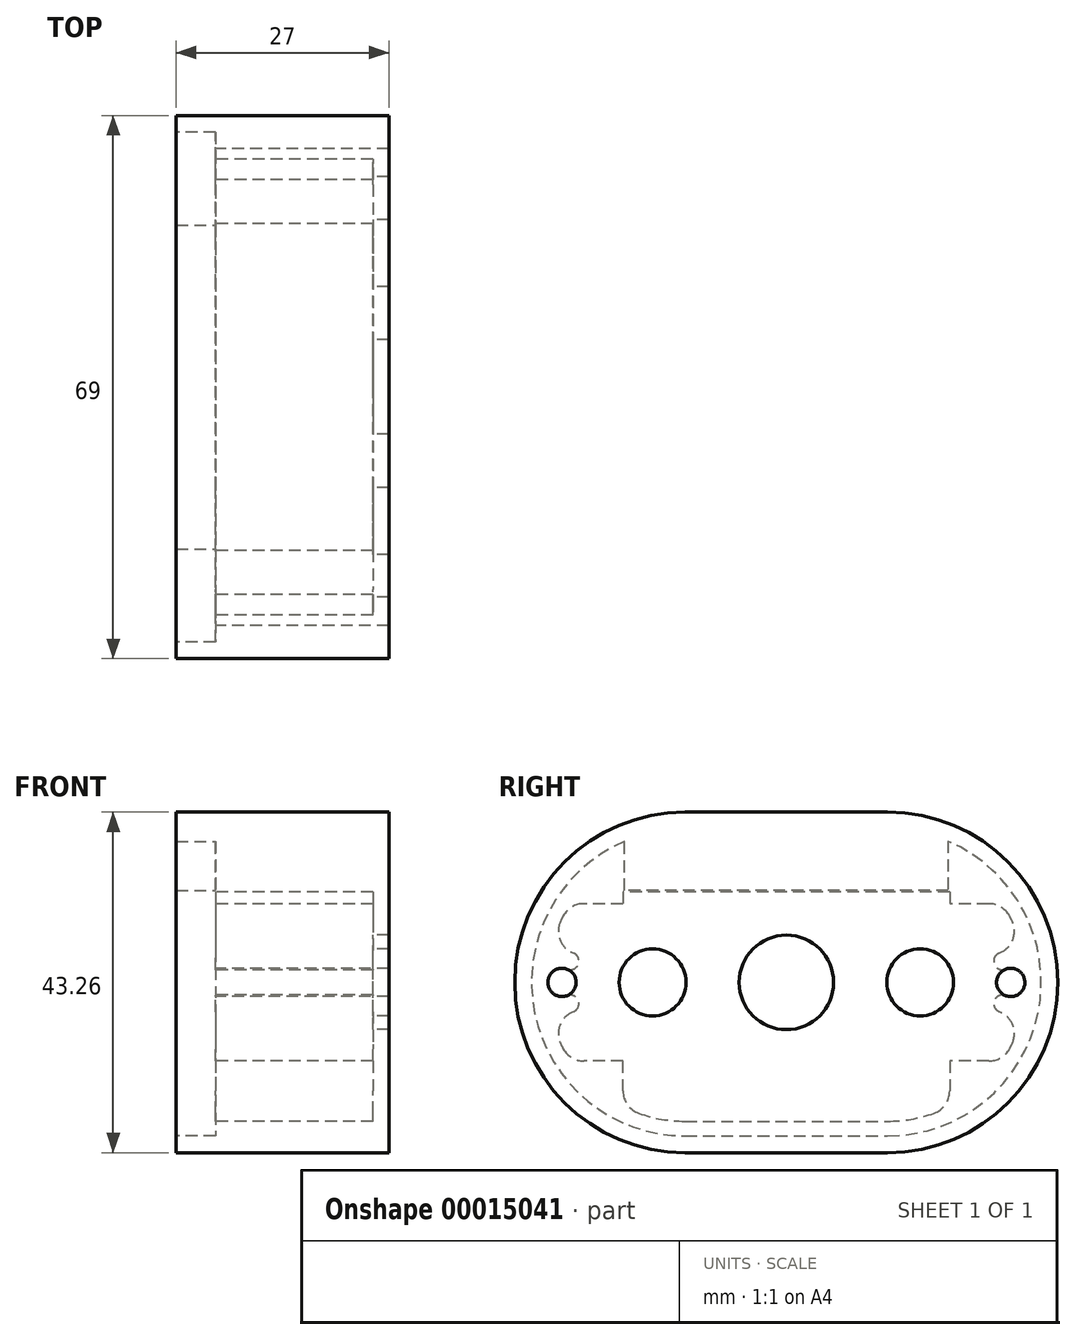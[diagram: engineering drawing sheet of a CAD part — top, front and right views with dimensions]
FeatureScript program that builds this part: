
annotation { "Feature Type Name" : "Feature", "Feature Type Description" : "" }
export const myFeature = defineFeature(function(context is Context, id is Id, definition is map)
    precondition{}
    {
        {
            var Q0;
            Q0=qCreatedBy(makeId("Right.planeOp"),FACE);
            var sketch = newSketch(context, id + "F0", { "sketchPlane" : qUnion([Q0])});
            skLineSegment(sketch, "E0.rect.bottom", {"start": v(23.75, -10) * mm, "end": v(-23.75, -10) * mm});
            skLineSegment(sketch, "E0.rect.top", {"start": v(23.75, 10) * mm, "end": v(-23.75, 10) * mm});
            skLineSegment(sketch, "E0.rect.left", {"start": v(23.75, -10) * mm, "end": v(23.75, 10) * mm});
            skLineSegment(sketch, "E0.rect.right", {"start": v(-23.75, -10) * mm, "end": v(-23.75, 10) * mm});
            skLineSegment(sketch, "E1.bottom", {"start": v(-23.75, 10) * mm, "end": v(23.75, 10) * mm});
            skLineSegment(sketch, "E1.top", {"start": v(-23.75, 12.1) * mm, "end": v(23.75, 12.1) * mm});
            skLineSegment(sketch, "E1.left", {"start": v(-23.75, 10) * mm, "end": v(-23.75, 12.1) * mm});
            skLineSegment(sketch, "E1.right", {"start": v(23.75, 10) * mm, "end": v(23.75, 12.1) * mm});
            skLineSegment(sketch, "E2.bottom", {"start": v(-23.75, -10) * mm, "end": v(23.75, -10) * mm});
            skLineSegment(sketch, "E2.top", {"start": v(-23.75, -12.1) * mm, "end": v(23.75, -12.1) * mm});
            skLineSegment(sketch, "E2.left", {"start": v(-23.75, -10) * mm, "end": v(-23.75, -12.1) * mm});
            skLineSegment(sketch, "E2.right", {"start": v(23.75, -10) * mm, "end": v(23.75, -12.1) * mm});
            skLineSegment(sketch, "E3", {"start": v(-23.75, 10) * mm, "end": v(0, 0) * mm, "construction": true});
            skLineSegment(sketch, "E4", {"start": v(0, 0) * mm, "end": v(23.75, -10) * mm, "construction": true});
            skLineSegment(sketch, "E5", {"start": v(-23.75, -10) * mm, "end": v(-20.75, -10) * mm});
            skLineSegment(sketch, "E6", {"start": v(-20.75, -10) * mm, "end": v(-20.75, -8) * mm});
            skLineSegment(sketch, "E7", {"start": v(-20.75, -8) * mm, "end": v(-25.75, -8) * mm});
            skLineSegment(sketch, "E8", {"start": v(-25.75, -8) * mm, "end": v(-25.75, -14.1) * mm});
            skLineSegment(sketch, "E9", {"start": v(-25.75, -14.1) * mm, "end": v(-20.75, -14.1) * mm});
            skLineSegment(sketch, "E10", {"start": v(-20.75, -14.1) * mm, "end": v(-20.75, -17.1) * mm});
            skLineSegment(sketch, "E11", {"start": v(-20.75, -17.1) * mm, "end": v(20.75, -17.1) * mm});
            skLineSegment(sketch, "E12", {"start": v(20.75, -17.1) * mm, "end": v(20.75, -14.1) * mm});
            skLineSegment(sketch, "E13", {"start": v(20.75, -14.1) * mm, "end": v(25.75, -14.1) * mm});
            skLineSegment(sketch, "E14", {"start": v(25.75, -14.1) * mm, "end": v(25.75, -8) * mm});
            skLineSegment(sketch, "E15", {"start": v(25.75, -8) * mm, "end": v(20.75, -8) * mm});
            skLineSegment(sketch, "E16", {"start": v(20.75, -8) * mm, "end": v(20.75, -10) * mm});
            skLineSegment(sketch, "E17", {"start": v(-20.75, 10) * mm, "end": v(-20.75, 8) * mm});
            skLineSegment(sketch, "E18", {"start": v(-20.75, 8) * mm, "end": v(-25.75, 8) * mm});
            skLineSegment(sketch, "E19", {"start": v(-25.75, 8) * mm, "end": v(-25.75, 14.1) * mm});
            skLineSegment(sketch, "E20", {"start": v(-25.75, 14.1) * mm, "end": v(-20.75, 14.1) * mm});
            skLineSegment(sketch, "E21", {"start": v(-20.75, 14.1) * mm, "end": v(-20.75, 12.1) * mm});
            skLineSegment(sketch, "E22", {"start": v(20.75, 12.1) * mm, "end": v(20.75, 14.1) * mm});
            skLineSegment(sketch, "E23", {"start": v(20.75, 14.1) * mm, "end": v(25.75, 14.1) * mm});
            skLineSegment(sketch, "E24", {"start": v(25.75, 14.1) * mm, "end": v(25.75, 8) * mm});
            skLineSegment(sketch, "E25", {"start": v(25.75, 8) * mm, "end": v(20.75, 8) * mm});
            skLineSegment(sketch, "E26", {"start": v(20.75, 8) * mm, "end": v(20.75, 10) * mm});
            skCircle(sketch, "E27", {"center": v(-28.5, 0) * mm, "radius": 1.25 * mm});
            skCircle(sketch, "E28", {"center": v(28.5, 0) * mm, "radius": 1.25 * mm});
            skLineSegment(sketch, "E29", {"start": v(-28.5, 0) * mm, "end": v(0, 0) * mm, "construction": true});
            skLineSegment(sketch, "E30", {"start": v(28.5, 0) * mm, "end": v(0, 0) * mm, "construction": true});
            skLineSegment(sketch, "E31.bottom", {"start": v(-25.75, -14.1) * mm, "end": v(25.75, -14.1) * mm});
            skLineSegment(sketch, "E31.top", {"start": v(-25.75, -19.1) * mm, "end": v(25.75, -19.1) * mm});
            skLineSegment(sketch, "E31.left", {"start": v(-25.75, -14.1) * mm, "end": v(-25.75, -19.1) * mm});
            skLineSegment(sketch, "E31.right", {"start": v(25.75, -14.1) * mm, "end": v(25.75, -19.1) * mm});
            skArc(sketch, "E32", {"start": v(-12.87, 19.1) * mm, "mid": v(-31.97, 0) * mm, "end": v(-12.87, -19.1) * mm});
            skArc(sketch, "E33", {"start": v(12.87, -19.1) * mm, "mid": v(31.97, 0) * mm, "end": v(12.87, 19.1) * mm});
            skLineSegment(sketch, "E34", {"start": v(-12.87, 19.1) * mm, "end": v(-12.87, 0) * mm, "construction": true});
            skLineSegment(sketch, "E35", {"start": v(-12.87, -19.1) * mm, "end": v(-12.87, 0) * mm, "construction": true});
            skLineSegment(sketch, "E36", {"start": v(12.87, 0) * mm, "end": v(12.87, 19.1) * mm, "construction": true});
            skLineSegment(sketch, "E37", {"start": v(12.87, 0) * mm, "end": v(12.87, -19.1) * mm, "construction": true});
            skLineSegment(sketch, "E38.rect.bottom", {"start": v(24.5, -9.5) * mm, "end": v(11.5, -9.5) * mm});
            skLineSegment(sketch, "E38.rect.top", {"start": v(24.5, 9.5) * mm, "end": v(11.5, 9.5) * mm});
            skLineSegment(sketch, "E38.rect.left", {"start": v(24.5, -9.5) * mm, "end": v(24.5, 9.5) * mm});
            skLineSegment(sketch, "E38.rect.right", {"start": v(11.5, -9.5) * mm, "end": v(11.5, 9.5) * mm});
            skPoint(sketch, "E38.rect.middle", {"position": v(18, 0) * mm});
            skLineSegment(sketch, "E39.rect.bottom", {"start": v(3.75, -7.75) * mm, "end": v(-18.75, -7.75) * mm});
            skLineSegment(sketch, "E39.rect.top", {"start": v(3.75, 7.75) * mm, "end": v(-18.75, 7.75) * mm});
            skLineSegment(sketch, "E39.rect.left", {"start": v(3.75, -7.75) * mm, "end": v(3.75, 7.75) * mm});
            skLineSegment(sketch, "E39.rect.right", {"start": v(-18.75, -7.75) * mm, "end": v(-18.75, 7.75) * mm});
            skPoint(sketch, "E39.rect.middle", {"position": v(-7.5, 0) * mm});
            skCircle(sketch, "E40", {"center": v(-22.25, 0) * mm, "radius": 1.75 * mm});
            skCircle(sketch, "E41", {"center": v(7.25, 0) * mm, "radius": 1.75 * mm});
            skLineSegment(sketch, "E42", {"start": v(-22.25, 0) * mm, "end": v(-7.5, 0) * mm, "construction": true});
            skLineSegment(sketch, "E43", {"start": v(-7.5, 0) * mm, "end": v(7.25, 0) * mm, "construction": true});
            skLineSegment(sketch, "E44.rect.bottom", {"start": v(10.5, 8.5) * mm, "end": v(-25.5, 8.5) * mm});
            skLineSegment(sketch, "E44.rect.top", {"start": v(10.5, -8.5) * mm, "end": v(-25.5, -8.5) * mm});
            skLineSegment(sketch, "E44.rect.left", {"start": v(10.5, 8.5) * mm, "end": v(10.5, -8.5) * mm});
            skLineSegment(sketch, "E44.rect.right", {"start": v(-25.5, 8.5) * mm, "end": v(-25.5, -8.5) * mm});
            skLineSegment(sketch, "E45.rect.bottom", {"start": v(25.5, 10.5) * mm, "end": v(10.5, 10.5) * mm});
            skLineSegment(sketch, "E45.rect.top", {"start": v(25.5, -10.5) * mm, "end": v(10.5, -10.5) * mm});
            skLineSegment(sketch, "E45.rect.left", {"start": v(25.5, 10.5) * mm, "end": v(25.5, -10.5) * mm});
            skLineSegment(sketch, "E45.rect.right", {"start": v(10.5, 10.5) * mm, "end": v(10.5, -10.5) * mm});
            skLineSegment(sketch, "E46", {"start": v(-20.75, 14.1) * mm, "end": v(-20.75, 17.4) * mm});
            skLineSegment(sketch, "E47", {"start": v(20.75, 14.1) * mm, "end": v(20.75, 17.4) * mm});
            skSolve(sketch);
        }
        {
            var Q0;
            Q0=qCreatedBy(makeId("Right.planeOp"),FACE);
            var sketch = newSketch(context, id + "F1", { "sketchPlane" : qUnion([Q0])});
            skArc(sketch, "E48", {"start": v(-12.87, 19.5) * mm, "mid": v(-32.37, 0) * mm, "end": v(-12.87, -19.5) * mm});
            skArc(sketch, "E49", {"start": v(12.87, -19.5) * mm, "mid": v(32.37, 0) * mm, "end": v(12.87, 19.5) * mm});
            skLineSegment(sketch, "E50", {"start": v(-12.87, 19.5) * mm, "end": v(12.87, 19.5) * mm});
            skLineSegment(sketch, "E51", {"start": v(-12.87, -19.5) * mm, "end": v(12.87, -19.5) * mm});
            skLineSegment(sketch, "E52.0", {"start": v(-12.87, 21.63) * mm, "end": v(12.87, 21.63) * mm});
            skArc(sketch, "E52.1", {"start": v(-12.87, 21.63) * mm, "mid": v(-34.5, 0) * mm, "end": v(-12.87, -21.63) * mm});
            skLineSegment(sketch, "E52.2", {"start": v(-12.87, -21.63) * mm, "end": v(12.87, -21.63) * mm});
            skArc(sketch, "E52.3", {"start": v(12.87, -21.63) * mm, "mid": v(34.5, 0) * mm, "end": v(12.87, 21.63) * mm});
            skPoint(sketch, "E53", {"position": v(-34.5, 0) * mm});
            skPoint(sketch, "E54", {"position": v(34.5, 0) * mm});
            skSolve(sketch);
        }
        {
            var Q0;
            Q0=qSketchRegion(id+"F1",true);
            extrude(context, id + "F2", {"entities" : qUnion([Q0]), "depth" : 5 * mm});
        }
        {
            var Q0;
            Q0=makeQuery(id+"F2.opExtrude","CAP_FACE",FACE,{"disambiguationData":[OSD([sQuery(id+"F1.wireOp",EDGE,"E48"),sQuery(id+"F1.wireOp",EDGE,"E49"),sQuery(id+"F1.wireOp",EDGE,"E50"),sQuery(id+"F1.wireOp",EDGE,"E51"),sQuery(id+"F1.wireOp",EDGE,"E52.0"),sQuery(id+"F1.wireOp",EDGE,"E52.1"),sQuery(id+"F1.wireOp",EDGE,"E52.2"),sQuery(id+"F1.wireOp",EDGE,"E52.3")])],"isStart":false});
            var sketch = newSketch(context, id + "F3", { "sketchPlane" : qUnion([Q0])});
            skLineSegment(sketch, "E55.0", {"start": v(-12.87, 17.63) * mm, "end": v(12.87, 17.63) * mm, "construction": true});
            skArc(sketch, "E55.1", {"start": v(-12.87, 17.63) * mm, "mid": v(-15.85, 17.38) * mm, "end": v(-18.75, 16.62) * mm, "construction": true});
            skLineSegment(sketch, "E55.2", {"start": v(-12.87, -17.63) * mm, "end": v(12.87, -17.63) * mm});
            skArc(sketch, "E55.3", {"start": v(12.87, -17.63) * mm, "mid": v(15.85, -17.38) * mm, "end": v(18.75, -16.62) * mm});
            skLineSegment(sketch, "E56.0", {"start": v(-12.87, 21.63) * mm, "end": v(12.87, 21.63) * mm});
            skArc(sketch, "E56.1", {"start": v(-12.87, 21.63) * mm, "mid": v(-34.5, 0) * mm, "end": v(-12.87, -21.63) * mm});
            skArc(sketch, "E56.2", {"start": v(12.87, -21.63) * mm, "mid": v(34.5, 0) * mm, "end": v(12.87, 21.63) * mm});
            skLineSegment(sketch, "E56.3", {"start": v(-12.87, -21.63) * mm, "end": v(12.87, -21.63) * mm});
            skArc(sketch, "E57", {"start": v(-27.85, 1.68) * mm, "mid": v(-30.3, 0) * mm, "end": v(-27.85, -1.68) * mm});
            skArc(sketch, "E58", {"start": v(27.85, -1.68) * mm, "mid": v(30.3, 0) * mm, "end": v(27.85, 1.68) * mm});
            skArc(sketch, "E59", {"start": v(27.05, 3.73) * mm, "mid": v(24.5, 0) * mm, "end": v(27.05, -3.73) * mm, "construction": true});
            skArc(sketch, "E60.trimOffspring", {"start": v(-28.65, -7.86) * mm, "mid": v(-28.5, -8.15) * mm, "end": v(-28.35, -8.44) * mm});
            skArc(sketch, "E61.trimOffspring", {"start": v(28.65, 7.86) * mm, "mid": v(28.5, 8.15) * mm, "end": v(28.35, 8.44) * mm});
            skPoint(sketch, "E62.visualSharp", {"position": v(-28.65, 7.86) * mm});
            skArc(sketch, "E62.filletArc", {"start": v(-28.65, 7.86) * mm, "mid": v(-28.76, 5.44) * mm, "end": v(-27.05, 3.73) * mm});
            skArc(sketch, "E63.filletArc", {"start": v(-27.05, -3.73) * mm, "mid": v(-28.76, -5.44) * mm, "end": v(-28.65, -7.86) * mm});
            skPoint(sketch, "E64.visualSharp", {"position": v(30.12, 3.66) * mm});
            skArc(sketch, "E64.filletArc", {"start": v(27.05, 3.73) * mm, "mid": v(28.76, 5.44) * mm, "end": v(28.65, 7.86) * mm});
            skPoint(sketch, "E65.visualSharp", {"position": v(30.12, -3.66) * mm});
            skArc(sketch, "E65.filletArc", {"start": v(28.65, -7.86) * mm, "mid": v(28.76, -5.44) * mm, "end": v(27.05, -3.73) * mm});
            skArc(sketch, "E66", {"start": v(-27.85, 1.68) * mm, "mid": v(-26.42, 2.3) * mm, "end": v(-27.05, 3.73) * mm});
            skArc(sketch, "E67", {"start": v(-27.05, -3.73) * mm, "mid": v(-26.42, -2.3) * mm, "end": v(-27.85, -1.68) * mm});
            skArc(sketch, "E68", {"start": v(27.05, 3.73) * mm, "mid": v(26.42, 2.3) * mm, "end": v(27.85, 1.68) * mm});
            skArc(sketch, "E69", {"start": v(27.85, -1.68) * mm, "mid": v(26.42, -2.3) * mm, "end": v(27.05, -3.73) * mm});
            skCircle(sketch, "E70", {"center": v(-28.5, 0) * mm, "radius": 1.8 * mm, "construction": true});
            skCircle(sketch, "E71", {"center": v(-28.5, 0) * mm, "radius": 4 * mm, "construction": true});
            skLineSegment(sketch, "E72.top", {"start": v(25.72, 10) * mm, "end": v(20.75, 10) * mm});
            skLineSegment(sketch, "E72.right", {"start": v(20.75, 13.8) * mm, "end": v(20.75, 10) * mm, "construction": true});
            skArc(sketch, "E73.trimOffspring", {"start": v(18.75, 16.62) * mm, "mid": v(15.85, 17.38) * mm, "end": v(12.87, 17.63) * mm, "construction": true});
            skPoint(sketch, "E74.visualSharp", {"position": v(20.75, 15.77) * mm});
            skArc(sketch, "E74.filletArc", {"start": v(20.75, 13.8) * mm, "mid": v(20.2, 15.53) * mm, "end": v(18.75, 16.62) * mm, "construction": true});
            skPoint(sketch, "E75.visualSharp", {"position": v(27.4, 10) * mm});
            skArc(sketch, "E75.filletArc", {"start": v(28.35, 8.44) * mm, "mid": v(27.25, 9.58) * mm, "end": v(25.72, 10) * mm});
            skLineSegment(sketch, "E76", {"start": v(25.72, -10) * mm, "end": v(20.75, -10) * mm});
            skLineSegment(sketch, "E77", {"start": v(20.75, -10) * mm, "end": v(20.75, -13.8) * mm});
            skArc(sketch, "E78.trimOffspring", {"start": v(28.35, -8.44) * mm, "mid": v(28.5, -8.15) * mm, "end": v(28.65, -7.86) * mm});
            skPoint(sketch, "E79.visualSharp", {"position": v(27.4, -10) * mm});
            skArc(sketch, "E79.filletArc", {"start": v(25.72, -10) * mm, "mid": v(27.25, -9.58) * mm, "end": v(28.35, -8.44) * mm});
            skPoint(sketch, "E80.visualSharp", {"position": v(20.75, -15.77) * mm});
            skArc(sketch, "E80.filletArc", {"start": v(18.75, -16.62) * mm, "mid": v(20.2, -15.53) * mm, "end": v(20.75, -13.8) * mm});
            skLineSegment(sketch, "E81", {"start": v(-20.75, -13.8) * mm, "end": v(-20.75, -10) * mm});
            skLineSegment(sketch, "E82", {"start": v(-20.75, -10) * mm, "end": v(-25.72, -10) * mm});
            skArc(sketch, "E83.trimOffspring", {"start": v(-18.75, -16.62) * mm, "mid": v(-15.85, -17.38) * mm, "end": v(-12.87, -17.63) * mm});
            skPoint(sketch, "E84.visualSharp", {"position": v(-20.75, -15.77) * mm});
            skArc(sketch, "E84.filletArc", {"start": v(-20.75, -13.8) * mm, "mid": v(-20.2, -15.53) * mm, "end": v(-18.75, -16.62) * mm});
            skPoint(sketch, "E85.visualSharp", {"position": v(-27.4, -10) * mm});
            skArc(sketch, "E85.filletArc", {"start": v(-28.35, -8.44) * mm, "mid": v(-27.25, -9.58) * mm, "end": v(-25.72, -10) * mm});
            skLineSegment(sketch, "E86", {"start": v(-20.75, 13.8) * mm, "end": v(-20.75, 10) * mm, "construction": true});
            skLineSegment(sketch, "E87", {"start": v(-20.75, 10) * mm, "end": v(-25.72, 10) * mm});
            skArc(sketch, "E88.trimOffspring", {"start": v(-28.35, 8.44) * mm, "mid": v(-28.5, 8.15) * mm, "end": v(-28.65, 7.86) * mm});
            skPoint(sketch, "E89.visualSharp", {"position": v(-27.4, 10) * mm});
            skArc(sketch, "E89.filletArc", {"start": v(-25.72, 10) * mm, "mid": v(-27.25, 9.58) * mm, "end": v(-28.35, 8.44) * mm});
            skPoint(sketch, "E90.visualSharp", {"position": v(-20.75, 15.77) * mm});
            skArc(sketch, "E90.filletArc", {"start": v(-18.75, 16.62) * mm, "mid": v(-20.2, 15.53) * mm, "end": v(-20.75, 13.8) * mm, "construction": true});
            skLineSegment(sketch, "E91", {"start": v(20.75, 11.5) * mm, "end": v(-20.75, 11.5) * mm});
            skLineSegment(sketch, "E92", {"start": v(20.75, 10) * mm, "end": v(20.75, 11.5) * mm, "construction": true});
            skLineSegment(sketch, "E93", {"start": v(20.75, 11.5) * mm, "end": v(20.75, 10) * mm});
            skLineSegment(sketch, "E94", {"start": v(-20.75, 11.5) * mm, "end": v(-20.75, 10) * mm});
            skLineSegment(sketch, "E95", {"start": v(20.55, 17.92) * mm, "end": v(20.55, 11.7) * mm});
            skLineSegment(sketch, "E96", {"start": v(20.55, 11.7) * mm, "end": v(-20.55, 11.7) * mm});
            skLineSegment(sketch, "E97", {"start": v(-20.55, 11.7) * mm, "end": v(-20.55, 17.92) * mm});
            skArc(sketch, "E98.0", {"start": v(20.55, 17.92) * mm, "mid": v(16.79, 19.1) * mm, "end": v(12.87, 19.5) * mm});
            skLineSegment(sketch, "E98.1", {"start": v(-12.87, 19.5) * mm, "end": v(12.87, 19.5) * mm});
            skArc(sketch, "E98.2", {"start": v(-12.87, 19.5) * mm, "mid": v(-16.79, 19.1) * mm, "end": v(-20.55, 17.92) * mm});
            skPoint(sketch, "E99.orphan", {"position": v(12.87, -19.5) * mm});
            skArc(sketch, "E100.trimOffspring", {"start": v(-32.33, 1.15) * mm, "mid": v(-27.05, -13.38) * mm, "end": v(-12.87, -19.5) * mm});
            skSolve(sketch);
        }
        {
            var Q0;
            Q0=qSketchRegion(id+"F3",true);
            extrude(context, id + "F4", {"entities" : qUnion([Q0]), "operationType" : NewBodyOperationType.ADD, "depth" : 20 * mm});
        }
        {
            var Q0;
            Q0=makeQuery(id+"F4.opExtrude","CAP_FACE",FACE,{"disambiguationData":[OSD([sQuery(id+"F3.wireOp",EDGE,"E55.0"),sQuery(id+"F3.wireOp",EDGE,"E55.1"),sQuery(id+"F3.wireOp",EDGE,"E55.2"),sQuery(id+"F3.wireOp",EDGE,"E55.3"),sQuery(id+"F3.wireOp",EDGE,"E56.0"),sQuery(id+"F3.wireOp",EDGE,"E56.1"),sQuery(id+"F3.wireOp",EDGE,"E56.2"),sQuery(id+"F3.wireOp",EDGE,"E56.3"),sQuery(id+"F3.wireOp",EDGE,"E57"),sQuery(id+"F3.wireOp",EDGE,"E58"),sQuery(id+"F3.wireOp",EDGE,"E60.trimOffspring"),sQuery(id+"F3.wireOp",EDGE,"E61.trimOffspring"),sQuery(id+"F3.wireOp",EDGE,"E62.filletArc"),sQuery(id+"F3.wireOp",EDGE,"E63.filletArc"),sQuery(id+"F3.wireOp",EDGE,"E64.filletArc"),sQuery(id+"F3.wireOp",EDGE,"E65.filletArc"),sQuery(id+"F3.wireOp",EDGE,"E66"),sQuery(id+"F3.wireOp",EDGE,"E67"),sQuery(id+"F3.wireOp",EDGE,"E68"),sQuery(id+"F3.wireOp",EDGE,"E69")])],"isStart":false});
            var sketch = newSketch(context, id + "F5", { "sketchPlane" : qUnion([Q0])});
            skCircle(sketch, "E101", {"center": v(0, 0) * mm, "radius": 6 * mm});
            skLineSegment(sketch, "E102", {"start": v(-17, 0) * mm, "end": v(0, 0) * mm, "construction": true});
            skLineSegment(sketch, "E103", {"start": v(0, 0) * mm, "end": v(17, 0) * mm, "construction": true});
            skCircle(sketch, "E104", {"center": v(-17, 0) * mm, "radius": 4.25 * mm});
            skCircle(sketch, "E105", {"center": v(17, 0) * mm, "radius": 4.25 * mm});
            skCircle(sketch, "E106", {"center": v(-28.5, 0) * mm, "radius": 1.8 * mm});
            skCircle(sketch, "E107", {"center": v(28.5, 0) * mm, "radius": 1.8 * mm});
            skLineSegment(sketch, "E108.0", {"start": v(-12.87, 21.63) * mm, "end": v(12.87, 21.63) * mm});
            skArc(sketch, "E108.1", {"start": v(12.87, -21.63) * mm, "mid": v(34.5, 0) * mm, "end": v(12.87, 21.63) * mm});
            skArc(sketch, "E108.2", {"start": v(-12.87, 21.63) * mm, "mid": v(-34.5, 0) * mm, "end": v(-12.87, -21.63) * mm});
            skLineSegment(sketch, "E108.3", {"start": v(-12.87, -21.63) * mm, "end": v(12.87, -21.63) * mm});
            skSolve(sketch);
        }
        {
            var Q0;
            Q0 = qSketchRegion(id + "F5", true);
            extrude(context, id + "F6", {"entities" : qUnion([Q0]), "operationType" : NewBodyOperationType.ADD, "depth" : 2 * mm});
        }
        {
            var Q0;
            Q0=makeQuery(id+"F6.boolean.opBoolean","SPLIT",FACE,{"disambiguationData":[TD([makeQuery(id+"F2.opExtrude","SWEPT_FACE",FACE,{"disambiguationData":[OSD([sQuery(id+"F1.wireOp",EDGE,"E48")])]})])],"derivedFrom":makeQuery(id+"F6.opExtrude","CAP_FACE",FACE,{"disambiguationData":[OSD([sQuery(id+"F5.wireOp",EDGE,"E101"),sQuery(id+"F5.wireOp",EDGE,"E104"),sQuery(id+"F5.wireOp",EDGE,"E105"),sQuery(id+"F5.wireOp",EDGE,"E106"),sQuery(id+"F5.wireOp",EDGE,"E107"),sQuery(id+"F5.wireOp",EDGE,"E108.0"),sQuery(id+"F5.wireOp",EDGE,"E108.1"),sQuery(id+"F5.wireOp",EDGE,"E108.2"),sQuery(id+"F5.wireOp",EDGE,"E108.3")])],"isStart":true})});
            var sketch = newSketch(context, id + "F7", { "sketchPlane" : qUnion([Q0])});
            skArc(sketch, "E109.1", {"start": v(-20.55, 17.92) * mm, "mid": v(-16.79, 19.1) * mm, "end": v(-12.87, 19.5) * mm});
            skLineSegment(sketch, "E109.2", {"start": v(12.87, 19.5) * mm, "end": v(-12.87, 19.5) * mm});
            skArc(sketch, "E109.3", {"start": v(12.87, 19.5) * mm, "mid": v(16.79, 19.1) * mm, "end": v(20.55, 17.92) * mm});
            skLineSegment(sketch, "E109.4", {"start": v(20.55, 11.7) * mm, "end": v(20.55, 17.92) * mm});
            skLineSegment(sketch, "E109.5", {"start": v(-20.55, 17.92) * mm, "end": v(-20.55, 11.7) * mm});
            skLineSegment(sketch, "E109.6", {"start": v(-20.55, 11.7) * mm, "end": v(20.55, 11.7) * mm});
            skSolve(sketch);
        }
        {
            var Q0;
            Q0=makeQuery(id+"F7.imprint","IMPRINT",FACE,{"disambiguationData":[TD([[makeQuery(id+"F7.imprint","IMPRINT",EDGE,{"derivedFrom":sQuery(id+"F7.wireOp",EDGE,"E109.1")}),-1.0]])]});
            extrude(context, id + "F8", {"entities" : qUnion([Q0]), "operationType" : NewBodyOperationType.ADD, "depth" : 25 * mm});
        }
    });
